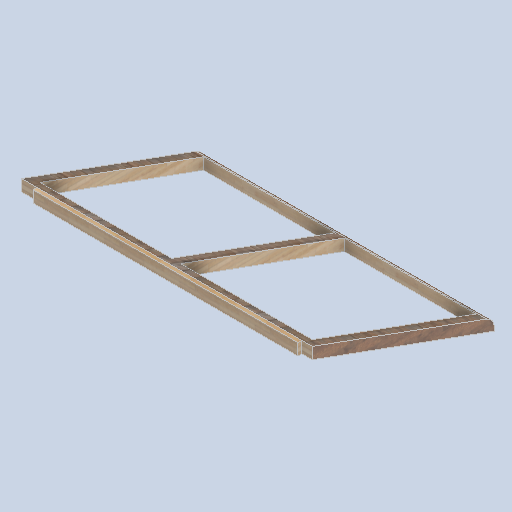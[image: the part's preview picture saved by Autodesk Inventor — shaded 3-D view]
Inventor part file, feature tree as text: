
AUTODESK INVENTOR PART (.ipt)
format: ipt  version: 2024.2 (Build 282272000, 272)  size: 169,984 bytes
history: native  units: in
note: dims shown in document units (in); Inventor stores cm internally (conversion verified against a paired STEP export)
features: sketch x6, other x3, plane x2
ambient origin geometry x8: Origin, YZ Plane, XZ Plane, XY Plane, X Axis, Y Axis, Z Axis, Center Point
bodies: Solid1 (feature_tree)
feature tree (11):
  other  "side_curve_frame_02.ipt"
  other  "Solid1::side_curve_frame_02.ipt"
  other  "TaggingFeature1"
  sketch  "Sketch1"  dims[d0=0.3937in]
  sketch  "Sketch2"
  sketch  "Sketch3"
  sketch  "Sketch4"
  sketch  "Sketch5"
  sketch  "Sketch6"
  plane  "Work Plane1"
  plane  "Work Plane2"
